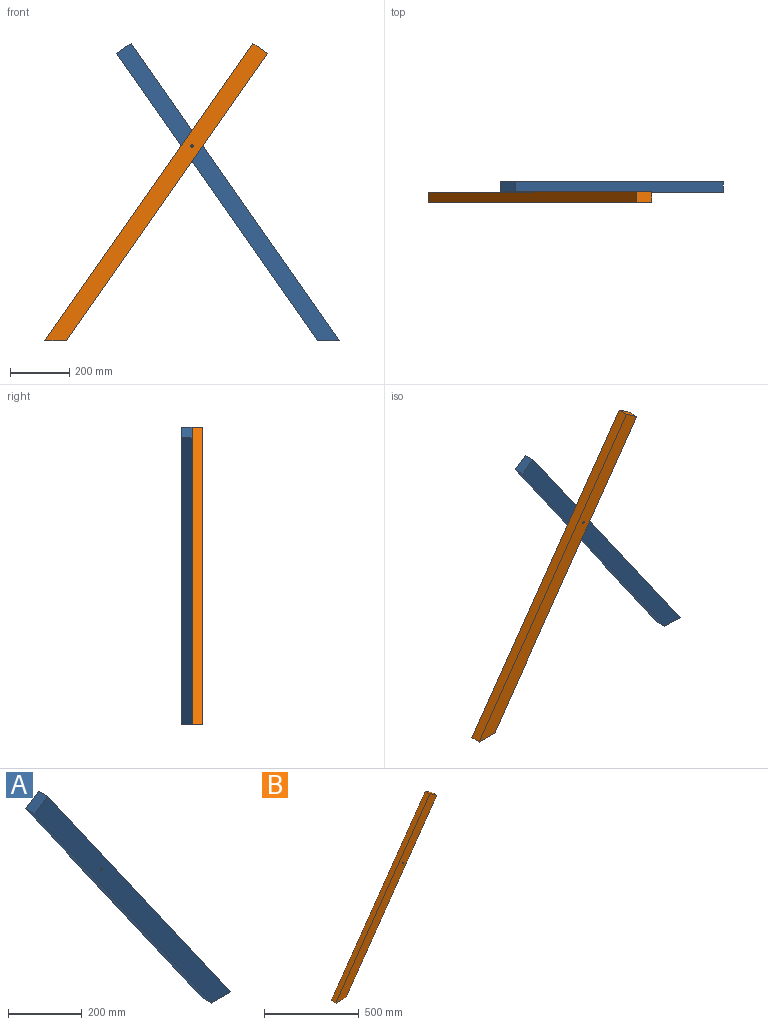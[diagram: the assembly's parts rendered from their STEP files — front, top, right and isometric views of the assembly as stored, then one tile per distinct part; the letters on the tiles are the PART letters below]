
ASSEMBLY  parts=2 mates=1
PART A: 7 faces, bbox 749.5x35x1000.2 mm
  f0: plane 49.15x35mm, normal (-0.57,0,0.82), area 2100mm2, adj f1,f4,f5,f6
  f1: plane 965.78x676.24mm, normal (-0.82,0,-0.57), area 41264.8mm2, adj f0,f2,f5,f6
  f2: plane 73.25x35mm, normal (0,0,-1), area 2563.6mm2, adj f1,f4,f5,f6
  f3: cylinder r=4mm len=35mm, axis (0,1,0), area 879.6mm2, adj f5,f6
  f4: plane 1000.19x700.34mm, normal (0.82,0,0.57), area 42735.2mm2, adj f0,f2,f5,f6
  f5: plane 1000.19x749.49mm, normal (0,-1,0), area 71949.7mm2, adj f0,f1,f2,f3,f4
  f6: plane 1000.19x749.49mm, normal (0,1,0), area 71949.7mm2, adj f0,f1,f2,f3,f4
PART B: 7 faces, bbox 749.5x35x1000.2 mm
  f0: plane 49.15x35mm, normal (0.57,0,0.82), area 2100mm2, adj f1,f3,f5,f6
  f1: plane 1000.19x700.34mm, normal (-0.82,0,0.57), area 42735.2mm2, adj f0,f2,f5,f6
  f2: plane 73.25x35mm, normal (0,0,-1), area 2563.6mm2, adj f1,f3,f5,f6
  f3: plane 965.78x676.24mm, normal (0.82,0,-0.57), area 41264.8mm2, adj f0,f2,f5,f6
  f4: cylinder r=4mm len=35mm, axis (0,1,0), area 879.6mm2, adj f5,f6
  f5: plane 1000.19x749.49mm, normal (0,-1,0), area 71949.7mm2, adj f0,f1,f2,f3,f4
  f6: plane 1000.19x749.49mm, normal (0,1,0), area 71949.7mm2, adj f0,f1,f2,f3,f4
PLACE A t=(-553.83,-155.1,-227.3)mm
PLACE B t=(-553.83,-190.1,-227.3)mm
MATE revolute A.f3 <-> B.f4  axis (0,-1,0) through (-553.83,-190.1,428.02)mm
